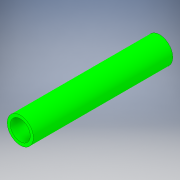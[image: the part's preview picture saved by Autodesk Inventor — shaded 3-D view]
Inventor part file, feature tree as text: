
AUTODESK INVENTOR PART (.ipt)
format: ipt  version: 2018 (Build 220112000, 112)  size: 106,496 bytes
history: native  units: in
note: dims shown in document units (in); Inventor stores cm internally (conversion verified against a paired STEP export)
features: extrude x1, sketch x1
ambient origin geometry x8: Origin, YZ Plane, XZ Plane, XY Plane, X Axis, Y Axis, Z Axis, Center Point
bodies: Solid1 (feature_tree)
feature tree (2):
  extrude  "Extrusion1"  Depth=7.0in
  sketch  "Sketch1"  dims[d0=1.315in d1=1.0in d2=7.0in d3=0.0in]
